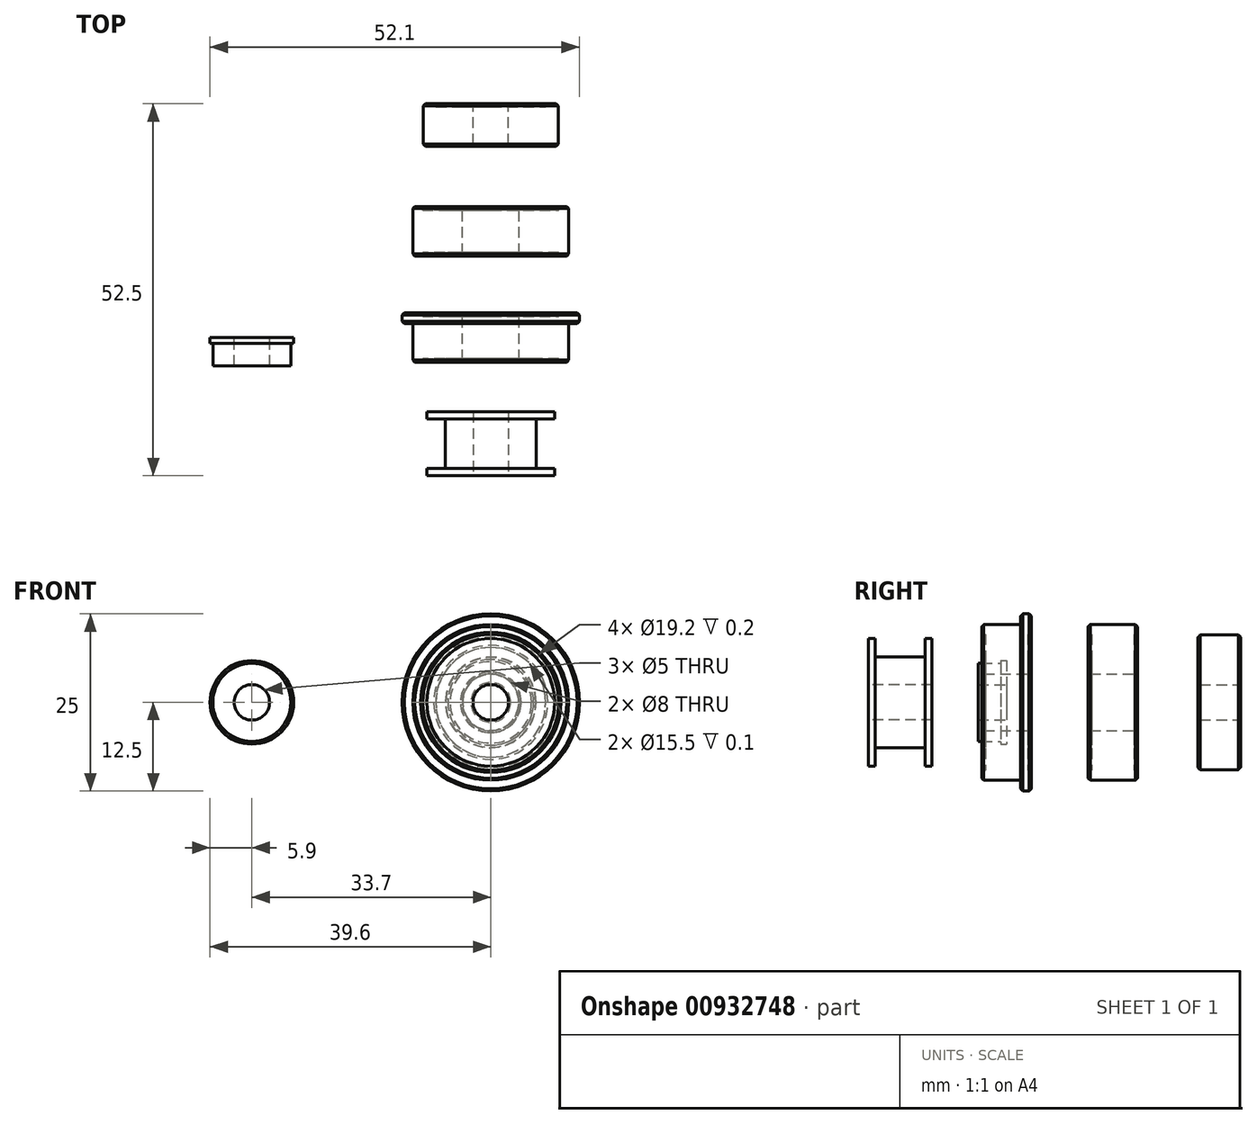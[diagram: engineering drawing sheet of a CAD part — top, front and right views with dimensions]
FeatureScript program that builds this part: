
annotation { "Feature Type Name" : "Feature", "Feature Type Description" : "" }
export const myFeature = defineFeature(function(context is Context, id is Id, definition is map)
    precondition{}
    {
        {
            var Q0;
            Q0=qCreatedBy(makeId("Right.planeOp"),FACE);
            var sketch = newSketch(context, id + "F0", { "sketchPlane" : qUnion([Q0])});
            skLineSegment(sketch, "E0", {"start": v(3.3, 0) * mm, "end": v(-12.28, 0) * mm, "construction": true});
            skLineSegment(sketch, "E1", {"start": v(0, 5.9) * mm, "end": v(-0.8, 5.9) * mm});
            skLineSegment(sketch, "E2", {"start": v(-0.8, 5.9) * mm, "end": v(-0.8, 5.5) * mm});
            skLineSegment(sketch, "E3", {"start": v(-0.8, 5.5) * mm, "end": v(-4, 5.5) * mm});
            skLineSegment(sketch, "E4", {"start": v(-4, 5.5) * mm, "end": v(-4, 2.5) * mm});
            skLineSegment(sketch, "E5", {"start": v(-4, 2.5) * mm, "end": v(0, 2.5) * mm});
            skLineSegment(sketch, "E6", {"start": v(0, 2.5) * mm, "end": v(0, 5.9) * mm});
            skSolve(sketch);
        }
        {
            var Q0;
            Q0=qSketchRegion(id+"F0",true);
            var Q1;
            Q1=sQuery(id+"F0.wireOp",EDGE,"E0");
            revolve(context, id + "F1", {"surfaceOperationType" : NewSurfaceOperationType.NEW, "entities" : qUnion([Q0]), "axis" : qUnion([Q1]), "revolveType" : RevolveType.FULL});
        }
        {
            var Q0;
            Q0=makeQuery(id+"F1.opRevolve","SWEPT_BODY",BODY,{"disambiguationData":[OSD([sQuery(id+"F0.wireOp",EDGE,"E1"),sQuery(id+"F0.wireOp",EDGE,"E2"),sQuery(id+"F0.wireOp",EDGE,"E3"),sQuery(id+"F0.wireOp",EDGE,"E4"),sQuery(id+"F0.wireOp",EDGE,"E5"),sQuery(id+"F0.wireOp",EDGE,"E6")])]});
            transform(context, id + "F2", {"entities" : qUnion([Q0]), "transformType" : TransformType.TRANSLATION_3D, "dx" : -33.7 * mm, "dy" : 0 * mm, "dz" : 0 * mm, "makeCopy" : false});
        }
        {
            var Q0;
            Q0=qCreatedBy(makeId("Right.planeOp"),FACE);
            var sketch = newSketch(context, id + "F3", { "sketchPlane" : qUnion([Q0])});
            skLineSegment(sketch, "E7", {"start": v(-3.5, 11) * mm, "end": v(2, 11) * mm});
            skLineSegment(sketch, "E8", {"start": v(2, 11) * mm, "end": v(2, 12.5) * mm});
            skLineSegment(sketch, "E9", {"start": v(2, 12.5) * mm, "end": v(3.5, 12.5) * mm});
            skLineSegment(sketch, "E10", {"start": v(3.5, 12.5) * mm, "end": v(3.5, 9.6) * mm});
            skLineSegment(sketch, "E11", {"start": v(3.5, 9.6) * mm, "end": v(3, 9.6) * mm});
            skLineSegment(sketch, "E12", {"start": v(3, 9.6) * mm, "end": v(3, 6.05) * mm});
            skLineSegment(sketch, "E13", {"start": v(3, 6.05) * mm, "end": v(3.5, 6.05) * mm});
            skLineSegment(sketch, "E14", {"start": v(3.5, 6.05) * mm, "end": v(3.5, 4) * mm});
            skLineSegment(sketch, "E15", {"start": v(3.5, 4) * mm, "end": v(-3.5, 4) * mm});
            skLineSegment(sketch, "E16", {"start": v(-3.5, 4) * mm, "end": v(-3.5, 6.05) * mm});
            skLineSegment(sketch, "E17", {"start": v(-3.5, 6.05) * mm, "end": v(-3, 6.05) * mm});
            skLineSegment(sketch, "E18", {"start": v(-3, 6.05) * mm, "end": v(-3, 9.6) * mm});
            skLineSegment(sketch, "E19", {"start": v(-3, 9.6) * mm, "end": v(-3.5, 9.6) * mm});
            skLineSegment(sketch, "E20", {"start": v(-3.5, 9.6) * mm, "end": v(-3.5, 11) * mm});
            skLineSegment(sketch, "E21", {"start": v(-3.5, 4) * mm, "end": v(0, 0) * mm, "construction": true});
            skLineSegment(sketch, "E22", {"start": v(0, 0) * mm, "end": v(3.5, 4) * mm, "construction": true});
            skLineSegment(sketch, "E23", {"start": v(0, 0) * mm, "end": v(-6.1, 0) * mm, "construction": true});
            skLineSegment(sketch, "E24", {"start": v(0, 0) * mm, "end": v(15, 0) * mm, "construction": true});
            skLineSegment(sketch, "E25", {"start": v(15, 0) * mm, "end": v(11.5, 4) * mm, "construction": true});
            skLineSegment(sketch, "E26", {"start": v(11.5, 4) * mm, "end": v(18.5, 4) * mm});
            skLineSegment(sketch, "E27", {"start": v(18.5, 4) * mm, "end": v(15, 0) * mm, "construction": true});
            skLineSegment(sketch, "E28", {"start": v(11.5, 4) * mm, "end": v(11.5, 6.05) * mm});
            skLineSegment(sketch, "E29", {"start": v(11.5, 6.05) * mm, "end": v(12, 6.05) * mm});
            skLineSegment(sketch, "E30", {"start": v(12, 6.05) * mm, "end": v(12, 9.6) * mm});
            skLineSegment(sketch, "E31", {"start": v(12, 9.6) * mm, "end": v(11.5, 9.6) * mm});
            skLineSegment(sketch, "E32", {"start": v(11.5, 9.6) * mm, "end": v(11.5, 11) * mm});
            skLineSegment(sketch, "E33", {"start": v(11.5, 11) * mm, "end": v(18.5, 11) * mm});
            skLineSegment(sketch, "E34", {"start": v(18.5, 11) * mm, "end": v(18.5, 9.6) * mm});
            skLineSegment(sketch, "E35", {"start": v(18.5, 9.6) * mm, "end": v(18, 9.6) * mm});
            skLineSegment(sketch, "E36", {"start": v(18, 9.6) * mm, "end": v(18, 6.05) * mm});
            skLineSegment(sketch, "E37", {"start": v(18, 6.05) * mm, "end": v(18.5, 6.05) * mm});
            skLineSegment(sketch, "E38", {"start": v(18.5, 6.05) * mm, "end": v(18.5, 4) * mm});
            skLineSegment(sketch, "E39", {"start": v(15, 0) * mm, "end": v(30, 0) * mm, "construction": true});
            skLineSegment(sketch, "E40", {"start": v(30, 0) * mm, "end": v(27, 2.5) * mm, "construction": true});
            skLineSegment(sketch, "E41", {"start": v(27, 2.5) * mm, "end": v(33, 2.5) * mm});
            skLineSegment(sketch, "E42", {"start": v(33, 2.5) * mm, "end": v(30, 0) * mm, "construction": true});
            skLineSegment(sketch, "E43", {"start": v(27, 2.5) * mm, "end": v(27, 4.25) * mm});
            skLineSegment(sketch, "E44", {"start": v(27, 4.25) * mm, "end": v(27.4, 4.25) * mm});
            skLineSegment(sketch, "E45", {"start": v(27.4, 4.25) * mm, "end": v(27.4, 7.75) * mm});
            skLineSegment(sketch, "E46", {"start": v(27.4, 7.75) * mm, "end": v(27, 7.75) * mm});
            skLineSegment(sketch, "E47", {"start": v(27, 7.75) * mm, "end": v(27, 9.5) * mm});
            skLineSegment(sketch, "E48", {"start": v(27, 9.5) * mm, "end": v(33, 9.5) * mm});
            skLineSegment(sketch, "E49", {"start": v(33, 9.5) * mm, "end": v(33, 7.75) * mm});
            skLineSegment(sketch, "E50", {"start": v(33, 7.75) * mm, "end": v(32.6, 7.75) * mm});
            skLineSegment(sketch, "E51", {"start": v(32.6, 7.75) * mm, "end": v(32.6, 4.25) * mm});
            skLineSegment(sketch, "E52", {"start": v(32.6, 4.25) * mm, "end": v(33, 4.25) * mm});
            skLineSegment(sketch, "E53", {"start": v(33, 4.25) * mm, "end": v(33, 2.5) * mm});
            skSolve(sketch);
        }
        {
            var Q0;
            Q0 = qSketchRegion(id + "F3", true);
            var Q1;
            Q1=sQuery(id+"F3.wireOp",EDGE,"E23");
            revolve(context, id + "F4", {"surfaceOperationType" : NewSurfaceOperationType.NEW, "entities" : qUnion([Q0]), "axis" : qUnion([Q1]), "revolveType" : RevolveType.FULL});
        }
        {
            var Q0;
            Q0=makeQuery(id+"F4.opRevolve","SWEPT_EDGE",EDGE,{"disambiguationData":[OSD([sQuery(id+"F3.wireOp",EDGE,"E7"),sQuery(id+"F3.wireOp",EDGE,"E20")])]});
            var Q1;
            Q1=makeQuery(id+"F4.opRevolve","SWEPT_EDGE",EDGE,{"disambiguationData":[OSD([sQuery(id+"F3.wireOp",EDGE,"E17"),sQuery(id+"F3.wireOp",EDGE,"E18")])]});
            var Q2;
            Q2=makeQuery(id+"F4.opRevolve","SWEPT_EDGE",EDGE,{"disambiguationData":[OSD([sQuery(id+"F3.wireOp",EDGE,"E19"),sQuery(id+"F3.wireOp",EDGE,"E20")])]});
            var Q3;
            Q3=makeQuery(id+"F4.opRevolve","SWEPT_EDGE",EDGE,{"disambiguationData":[OSD([sQuery(id+"F3.wireOp",EDGE,"E15"),sQuery(id+"F3.wireOp",EDGE,"E16")])]});
            var Q4;
            Q4=makeQuery(id+"F4.opRevolve","SWEPT_EDGE",EDGE,{"disambiguationData":[OSD([sQuery(id+"F3.wireOp",EDGE,"E14"),sQuery(id+"F3.wireOp",EDGE,"E15")])]});
            var Q5;
            Q5=makeQuery(id+"F4.opRevolve","SWEPT_EDGE",EDGE,{"disambiguationData":[OSD([sQuery(id+"F3.wireOp",EDGE,"E8"),sQuery(id+"F3.wireOp",EDGE,"E9")])]});
            var Q6;
            Q6=makeQuery(id+"F4.opRevolve","SWEPT_EDGE",EDGE,{"disambiguationData":[OSD([sQuery(id+"F3.wireOp",EDGE,"E9"),sQuery(id+"F3.wireOp",EDGE,"E10")])]});
            var Q7;
            Q7=makeQuery(id+"F4.opRevolve","SWEPT_EDGE",EDGE,{"disambiguationData":[OSD([sQuery(id+"F3.wireOp",EDGE,"E10"),sQuery(id+"F3.wireOp",EDGE,"E11")])]});
            var Q8;
            Q8=makeQuery(id+"F4.opRevolve","SWEPT_EDGE",EDGE,{"disambiguationData":[OSD([sQuery(id+"F3.wireOp",EDGE,"E13"),sQuery(id+"F3.wireOp",EDGE,"E14")])]});
            var Q9;
            Q9=makeQuery(id+"F4.opRevolve","SWEPT_EDGE",EDGE,{"disambiguationData":[OSD([sQuery(id+"F3.wireOp",EDGE,"E32"),sQuery(id+"F3.wireOp",EDGE,"E33")])]});
            var Q10;
            Q10=makeQuery(id+"F4.opRevolve","SWEPT_EDGE",EDGE,{"disambiguationData":[OSD([sQuery(id+"F3.wireOp",EDGE,"E31"),sQuery(id+"F3.wireOp",EDGE,"E32")])]});
            var Q11;
            Q11=makeQuery(id+"F4.opRevolve","SWEPT_EDGE",EDGE,{"disambiguationData":[OSD([sQuery(id+"F3.wireOp",EDGE,"E28"),sQuery(id+"F3.wireOp",EDGE,"E29")])]});
            var Q12;
            Q12=makeQuery(id+"F4.opRevolve","SWEPT_EDGE",EDGE,{"disambiguationData":[OSD([sQuery(id+"F3.wireOp",EDGE,"E33"),sQuery(id+"F3.wireOp",EDGE,"E34")])]});
            var Q13;
            Q13=makeQuery(id+"F4.opRevolve","SWEPT_EDGE",EDGE,{"disambiguationData":[OSD([sQuery(id+"F3.wireOp",EDGE,"E47"),sQuery(id+"F3.wireOp",EDGE,"E48")])]});
            var Q14;
            Q14=makeQuery(id+"F4.opRevolve","SWEPT_EDGE",EDGE,{"disambiguationData":[OSD([sQuery(id+"F3.wireOp",EDGE,"E46"),sQuery(id+"F3.wireOp",EDGE,"E47")])]});
            var Q15;
            Q15=makeQuery(id+"F4.opRevolve","SWEPT_EDGE",EDGE,{"disambiguationData":[OSD([sQuery(id+"F3.wireOp",EDGE,"E43"),sQuery(id+"F3.wireOp",EDGE,"E44")])]});
            var Q16;
            Q16=makeQuery(id+"F4.opRevolve","SWEPT_EDGE",EDGE,{"disambiguationData":[OSD([sQuery(id+"F3.wireOp",EDGE,"E48"),sQuery(id+"F3.wireOp",EDGE,"E49")])]});
            var Q17;
            Q17=makeQuery(id+"F4.opRevolve","SWEPT_EDGE",EDGE,{"disambiguationData":[OSD([sQuery(id+"F3.wireOp",EDGE,"E34"),sQuery(id+"F3.wireOp",EDGE,"E35")])]});
            var Q18;
            Q18=makeQuery(id+"F4.opRevolve","SWEPT_EDGE",EDGE,{"disambiguationData":[OSD([sQuery(id+"F3.wireOp",EDGE,"E37"),sQuery(id+"F3.wireOp",EDGE,"E38")])]});
            var Q19;
            Q19=makeQuery(id+"F4.opRevolve","SWEPT_EDGE",EDGE,{"disambiguationData":[OSD([sQuery(id+"F3.wireOp",EDGE,"E26"),sQuery(id+"F3.wireOp",EDGE,"E38")])]});
            var Q20;
            Q20=makeQuery(id+"F4.opRevolve","SWEPT_EDGE",EDGE,{"disambiguationData":[OSD([sQuery(id+"F3.wireOp",EDGE,"E41"),sQuery(id+"F3.wireOp",EDGE,"E53")])]});
            var Q21;
            Q21=makeQuery(id+"F4.opRevolve","SWEPT_EDGE",EDGE,{"disambiguationData":[OSD([sQuery(id+"F3.wireOp",EDGE,"E52"),sQuery(id+"F3.wireOp",EDGE,"E53")])]});
            var Q22;
            Q22=makeQuery(id+"F4.opRevolve","SWEPT_EDGE",EDGE,{"disambiguationData":[OSD([sQuery(id+"F3.wireOp",EDGE,"E49"),sQuery(id+"F3.wireOp",EDGE,"E50")])]});
            var Q23;
            Q23=makeQuery(id+"F4.opRevolve","SWEPT_EDGE",EDGE,{"disambiguationData":[OSD([sQuery(id+"F3.wireOp",EDGE,"E41"),sQuery(id+"F3.wireOp",EDGE,"E43")])]});
            var Q24;
            Q24=makeQuery(id+"F4.opRevolve","SWEPT_EDGE",EDGE,{"disambiguationData":[OSD([sQuery(id+"F3.wireOp",EDGE,"E26"),sQuery(id+"F3.wireOp",EDGE,"E28")])]});
            chamfer(context, id + "F5", {"entities" : qUnion([Q0, Q1, Q2, Q3, Q4, Q5, Q6, Q7, Q8, Q9, Q10, Q11, Q12, Q13, Q14, Q15, Q16, Q17, Q18, Q19, Q20, Q21, Q22, Q23, Q24]), "width" : 0.3 * mm, "tangentPropagation" : true});
        }
        {
            var Q0;
            Q0=qCreatedBy(makeId("Right.planeOp"),FACE);
            var sketch = newSketch(context, id + "F6", { "sketchPlane" : qUnion([Q0])});
            skLineSegment(sketch, "E54", {"start": v(0, 0) * mm, "end": v(23.97, 0) * mm, "construction": true});
            skLineSegment(sketch, "E55", {"start": v(-19.5, 9) * mm, "end": v(-19.5, 2.5) * mm});
            skLineSegment(sketch, "E56", {"start": v(-19.5, 2.5) * mm, "end": v(-10.5, 2.5) * mm});
            skLineSegment(sketch, "E57", {"start": v(-10.5, 2.5) * mm, "end": v(-10.5, 9) * mm});
            skLineSegment(sketch, "E58", {"start": v(-10.5, 9) * mm, "end": v(-11.5, 9) * mm});
            skLineSegment(sketch, "E59", {"start": v(-11.5, 9) * mm, "end": v(-11.5, 6.4) * mm});
            skLineSegment(sketch, "E60", {"start": v(-11.5, 6.4) * mm, "end": v(-18.5, 6.4) * mm});
            skLineSegment(sketch, "E61", {"start": v(-18.5, 6.4) * mm, "end": v(-18.5, 9) * mm});
            skLineSegment(sketch, "E62", {"start": v(-18.5, 9) * mm, "end": v(-19.5, 9) * mm});
            skSolve(sketch);
        }
        {
            var Q0;
            Q0 = qSketchRegion(id + "F6", true);
            var Q1;
            Q1=sQuery(id+"F6.wireOp",EDGE,"E54");
            revolve(context, id + "F7", {"surfaceOperationType" : NewSurfaceOperationType.NEW, "entities" : qUnion([Q0]), "axis" : qUnion([Q1]), "revolveType" : RevolveType.FULL});
        }
    });
